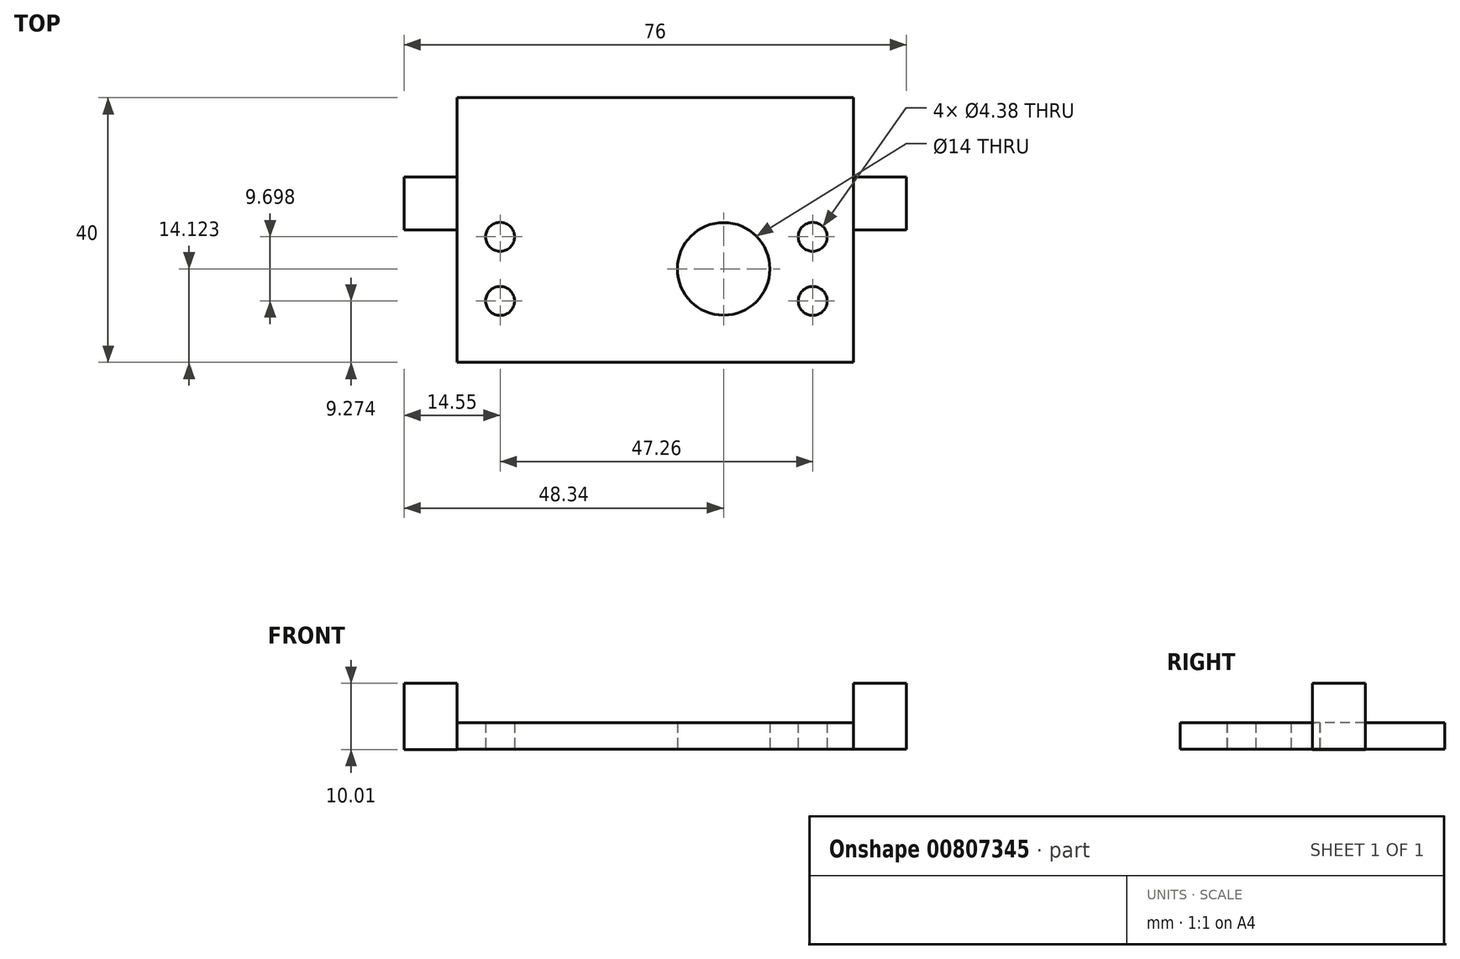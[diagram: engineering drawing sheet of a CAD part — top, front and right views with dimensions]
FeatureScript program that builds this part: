
annotation { "Feature Type Name" : "Feature", "Feature Type Description" : "" }
export const myFeature = defineFeature(function(context is Context, id is Id, definition is map)
    precondition{}
    {
        {
            var Q0;
            Q0=qCreatedBy(makeId("Top.planeOp"),FACE);
            var sketch = newSketch(context, id + "F0", { "sketchPlane" : qUnion([Q0])});
            skLineSegment(sketch, "E0.bottom", {"start": v(30, 20) * mm, "end": v(-30, 20) * mm});
            skLineSegment(sketch, "E0.top", {"start": v(30, -20) * mm, "end": v(-30, -20) * mm});
            skLineSegment(sketch, "E0.left", {"start": v(30, 20) * mm, "end": v(30, -20) * mm});
            skLineSegment(sketch, "E0.right", {"start": v(-30, 20) * mm, "end": v(-30, -20) * mm});
            skPoint(sketch, "E0.middle", {"position": v(0, 0) * mm});
            skLineSegment(sketch, "E1", {"start": v(-20.3, -16.02) * mm, "end": v(20, -16.02) * mm, "construction": true});
            skLineSegment(sketch, "E2", {"start": v(20, -16.02) * mm, "end": v(20, 3.8) * mm, "construction": true});
            skLineSegment(sketch, "E3", {"start": v(20, 3.8) * mm, "end": v(-20.3, 3.8) * mm, "construction": true});
            skLineSegment(sketch, "E4", {"start": v(-20.3, 3.8) * mm, "end": v(-20.3, -16.02) * mm, "construction": true});
            skCircle(sketch, "E5", {"center": v(10.34, -5.88) * mm, "radius": 7 * mm});
            skCircle(sketch, "E6", {"center": v(23.8, -1.03) * mm, "radius": 2.19 * mm});
            skLineSegment(sketch, "E7", {"start": v(10.34, -5.88) * mm, "end": v(-23.45, -5.88) * mm, "construction": true});
            skCircle(sketch, "E8", {"center": v(-23.45, -1.03) * mm, "radius": 2.19 * mm});
            skCircle(sketch, "E9.MirrorC", {"center": v(-23.45, -10.72) * mm, "radius": 2.19 * mm});
            skCircle(sketch, "E10.MirrorC", {"center": v(23.8, -10.73) * mm, "radius": 2.19 * mm});
            skSolve(sketch);
        }
        {
            var Q0;
            Q0=makeQuery(id+"F0.imprint","IMPRINT",FACE,{"disambiguationData":[TD([[makeQuery(id+"F0.imprint","IMPRINT",EDGE,{"derivedFrom":sQuery(id+"F0.wireOp",EDGE,"E0.bottom")}),1.0]])]});
            extrude(context, id + "F1", {"entities" : qUnion([Q0]), "depth" : 4 * mm, "offsetDistance" : 25 * mm});
        }
        {
            var Q0;
            Q0=makeQuery(id+"F1.opExtrude","CAP_FACE",FACE,{"disambiguationData":[OSD([sQuery(id+"F0.wireOp",EDGE,"E0.bottom"),sQuery(id+"F0.wireOp",EDGE,"E0.top"),sQuery(id+"F0.wireOp",EDGE,"E0.left"),sQuery(id+"F0.wireOp",EDGE,"E0.right"),sQuery(id+"F0.wireOp",EDGE,"zV5nhfBR-ClQT-OAvd-J1qB-6amOJ57wMCQx"),sQuery(id+"F0.wireOp",EDGE,"z1uIbwNq-yCL4-uMsc-NN3L-RcbKz70ZMMGy"),sQuery(id+"F0.wireOp",EDGE,"f28286a0-a375-4464-8e54-0388d9e939770.MirrorC"),sQuery(id+"F0.wireOp",EDGE,"11be3d1e-5166-4316-a3c9-6581ff42d7db0.MirrorC"),sQuery(id+"F0.wireOp",EDGE,"44e95fad-20e7-40f2-90ab-8aa8ba470f810.MirrorC")])],"isStart":true});
            var sketch = newSketch(context, id + "F2", { "sketchPlane" : qUnion([Q0])});
            skLineSegment(sketch, "E11", {"start": v(-16.25, 20) * mm, "end": v(-16.25, 0) * mm, "construction": true});
            skLineSegment(sketch, "E12", {"start": v(-16.25, 0) * mm, "end": v(-30, 0) * mm, "construction": true});
            skLineSegment(sketch, "E13.bottom", {"start": v(-30, 0) * mm, "end": v(-38, 0) * mm});
            skLineSegment(sketch, "E13.top", {"start": v(-30, -8) * mm, "end": v(-38, -8) * mm});
            skLineSegment(sketch, "E13.left", {"start": v(-30, 0) * mm, "end": v(-30, -8) * mm});
            skLineSegment(sketch, "E13.right", {"start": v(-38, 0) * mm, "end": v(-38, -8) * mm});
            skLineSegment(sketch, "E14.MirrorCS", {"start": v(30, -8) * mm, "end": v(38, -8) * mm});
            skLineSegment(sketch, "E15.MirrorCS", {"start": v(30, 0) * mm, "end": v(30, -8) * mm});
            skLineSegment(sketch, "E16.MirrorCS", {"start": v(30, 0) * mm, "end": v(38, 0) * mm});
            skLineSegment(sketch, "E17.MirrorCS", {"start": v(38, 0) * mm, "end": v(38, -8) * mm});
            skSolve(sketch);
        }
        {
            var Q0;
            Q0=makeQuery(id+"F2.imprint","IMPRINT",FACE,{"disambiguationData":[TD([[makeQuery(id+"F2.imprint","IMPRINT",EDGE,{"derivedFrom":sQuery(id+"F2.wireOp",EDGE,"E14.MirrorCS")}),1.0]])]});
            var Q1;
            Q1=makeQuery(id+"F2.imprint","IMPRINT",FACE,{"disambiguationData":[TD([[makeQuery(id+"F2.imprint","IMPRINT",EDGE,{"derivedFrom":sQuery(id+"F2.wireOp",EDGE,"E13.bottom")}),1.0]])]});
            extrude(context, id + "F3", {"entities" : qUnion([Q0, Q1]), "operationType" : NewBodyOperationType.ADD, "depth" : 10 * mm, "offsetDistance" : 25 * mm});
        }
        {
            var Q0;
            Q0=makeQuery(id+"F3.opExtrude","SWEPT_BODY",BODY,{"disambiguationData":[OSD([sQuery(id+"F2.wireOp",EDGE,"E14.MirrorCS"),sQuery(id+"F2.wireOp",EDGE,"E15.MirrorCS"),sQuery(id+"F2.wireOp",EDGE,"E16.MirrorCS"),sQuery(id+"F2.wireOp",EDGE,"E17.MirrorCS")])]});
            transform(context, id + "F4", {"entities" : qUnion([Q0]), "transformType" : TransformType.TRANSLATION_3D, "dx" : 0 * mm, "dy" : 0 * mm, "dz" : 10 * mm, "makeCopy" : false});
        }
        {
            var Q0;
            Q0=makeQuery(id+"F3.opExtrude","SWEPT_BODY",BODY,{"disambiguationData":[OSD([sQuery(id+"F2.wireOp",EDGE,"E13.bottom"),sQuery(id+"F2.wireOp",EDGE,"E13.top"),sQuery(id+"F2.wireOp",EDGE,"E13.left"),sQuery(id+"F2.wireOp",EDGE,"E13.right")])]});
            transform(context, id + "F5", {"entities" : qUnion([Q0]), "transformType" : TransformType.TRANSLATION_3D, "dx" : 0 * mm, "dy" : 0 * mm, "dz" : 9.98 * mm, "makeCopy" : false});
        }
    });
